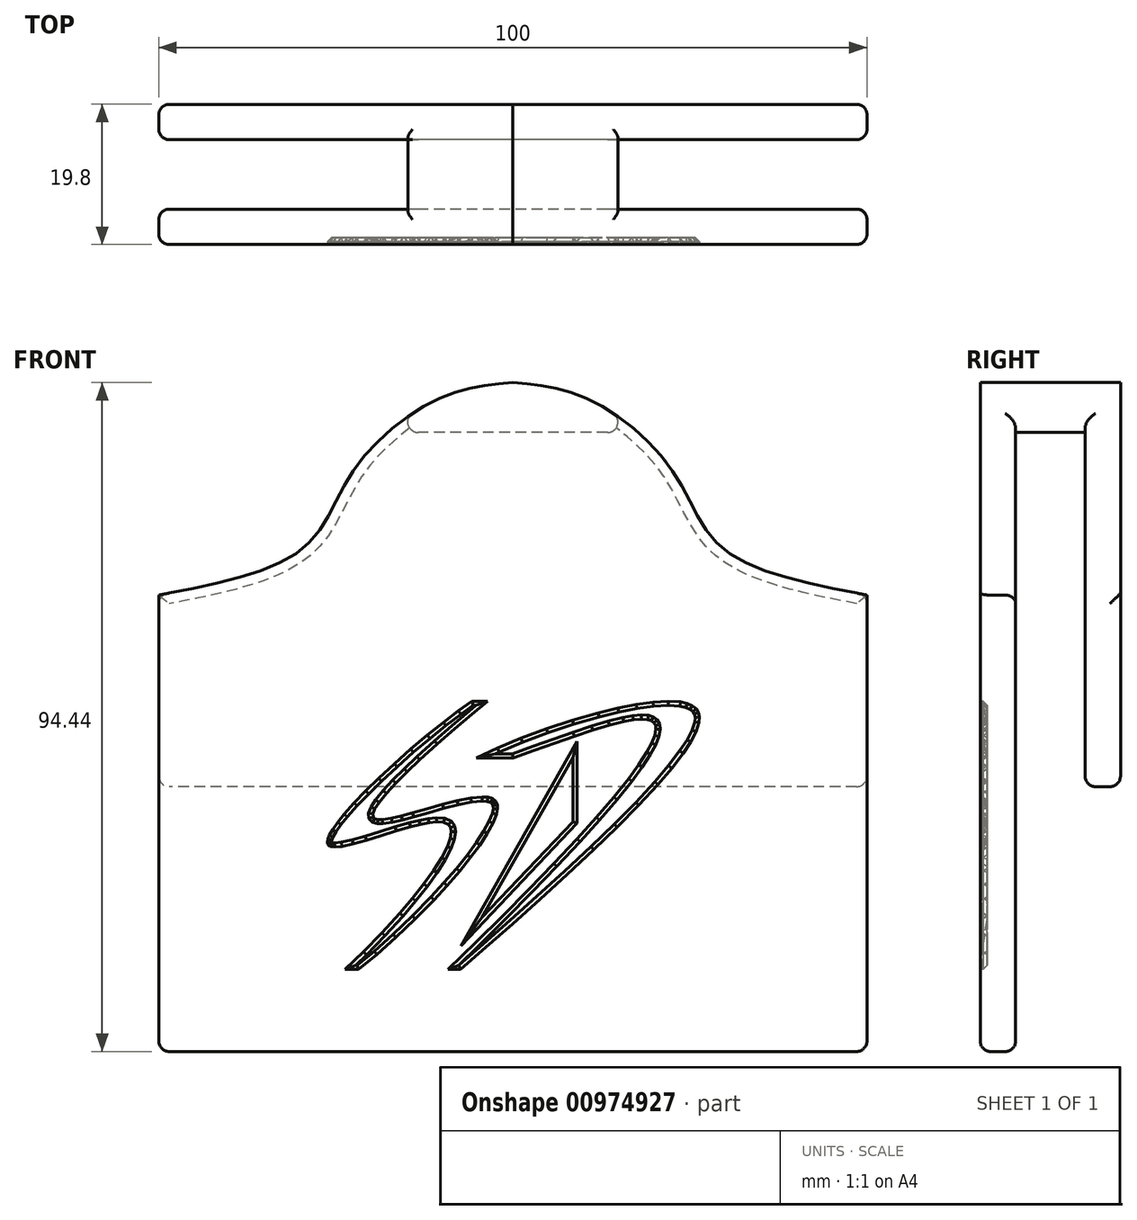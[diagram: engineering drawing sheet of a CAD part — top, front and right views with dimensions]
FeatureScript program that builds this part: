
annotation { "Feature Type Name" : "Feature", "Feature Type Description" : "" }
export const myFeature = defineFeature(function(context is Context, id is Id, definition is map)
    precondition{}
    {
        {
            var Q0;
            Q0=qCreatedBy(makeId("Right.planeOp"),FACE);
            var sketch = newSketch(context, id + "F0", { "sketchPlane" : qUnion([Q0])});
            skLineSegment(sketch, "E0.bottom", {"start": v(-5.4, 63.82) * mm, "end": v(3.6, 63.82) * mm, "construction": true});
            skLineSegment(sketch, "E0.top", {"start": v(-5.4, -23.18) * mm, "end": v(3.6, -23.18) * mm, "construction": true});
            skLineSegment(sketch, "E0.left", {"start": v(-5.4, 63.82) * mm, "end": v(-5.4, -23.18) * mm, "construction": true});
            skLineSegment(sketch, "E0.right", {"start": v(3.6, 63.82) * mm, "end": v(3.6, -23.18) * mm, "construction": true});
            skLineSegment(sketch, "E1", {"start": v(4, 14.22) * mm, "end": v(4, 64.22) * mm});
            skLineSegment(sketch, "E2", {"start": v(4, 64.22) * mm, "end": v(-5.8, 64.22) * mm});
            skLineSegment(sketch, "E3", {"start": v(-5.8, 64.22) * mm, "end": v(-5.8, -23.18) * mm});
            skLineSegment(sketch, "E4", {"start": v(-5.8, -23.18) * mm, "end": v(-10.8, -23.18) * mm});
            skLineSegment(sketch, "E5", {"start": v(-10.8, -23.18) * mm, "end": v(-10.8, 69.22) * mm});
            skLineSegment(sketch, "E6", {"start": v(-10.8, 69.22) * mm, "end": v(9, 69.22) * mm});
            skLineSegment(sketch, "E7", {"start": v(9, 69.22) * mm, "end": v(9, 14.22) * mm});
            skLineSegment(sketch, "E8", {"start": v(9, 14.22) * mm, "end": v(4, 14.22) * mm});
            skSolve(sketch);
        }
        {
            var Q0;
            Q0=makeQuery(id+"F0.imprint","IMPRINT",FACE,{"disambiguationData":[TD([[makeQuery(id+"F0.imprint","IMPRINT",EDGE,{"derivedFrom":sQuery(id+"F0.wireOp",EDGE,"E1")}),-1.0]])]});
            extrude(context, id + "F1", {"entities" : qUnion([Q0]), "depth" : 100 * mm, "offsetDistance" : 25 * mm});
        }
        {
            var Q0;
            Q0=makeQuery(id+"F1.opExtrude","SWEPT_FACE",FACE,{"disambiguationData":[OSD([sQuery(id+"F0.wireOp",EDGE,"E5")])]});
            var sketch = newSketch(context, id + "F2", { "sketchPlane" : qUnion([Q0])});
            skLineSegment(sketch, "E9", {"start": v(50, 69.22) * mm, "end": v(50, -23.18) * mm, "construction": true});
            skFitSpline(sketch, "E10", {"points": [v(0, 41.26) * mm, v(20.58, 48.07) * mm, v(27.58, 59) * mm, v(40.04, 69.22) * mm, v(50, 71.26) * mm], "startDerivative": vector(81.15, 15.4) * mm, "endDerivative": vector(46.63, 3.68) * mm});
            skFitSpline(sketch, "E11.MirrorCS", {"points": [v(100, 41.26) * mm, v(79.42, 48.07) * mm, v(72.42, 59) * mm, v(59.96, 69.22) * mm, v(50, 71.26) * mm], "startDerivative": vector(-81.15, 15.4) * mm, "endDerivative": vector(-46.63, 3.68) * mm});
            skSolve(sketch);
        }
        {
            var Q0;
            {var subQ0=sQuery(id+"F2.wireOp",EDGE,"E11.MirrorCS");var subQ1=sQuery(id+"F2.wireOp",EDGE,"E10");var subQ2=makeQuery(id+"F2.imprint","INTERSECT",VERTEX,{"derivedFrom":[subQ1,subQ0]});Q0=makeQuery(id+"F2.imprint","IMPRINT",FACE,{"disambiguationData":[TD([[makeQuery(id+"F2.imprint","IMPRINT",EDGE,{"disambiguationData":[TD([[subQ2,1.0]])],"derivedFrom":subQ1}),-1.0]])]});}
            var Q1;
            Q1=makeQuery(id+"F1.opExtrude","SWEPT_FACE",FACE,{"disambiguationData":[OSD([sQuery(id+"F0.wireOp",EDGE,"E7")])]});
            extrude(context, id + "F3", {"entities" : qUnion([Q0]), "operationType" : NewBodyOperationType.ADD, "endBound" : BoundingType.UP_TO_SURFACE, "oppositeDirection" : true, "depth" : 25 * mm, "endBoundEntityFace" : qUnion([Q1]), "offsetDistance" : 25 * mm});
        }
        {
            var Q0;
            {var subQ0=sQuery(id+"F2.wireOp",EDGE,"E10");var subQ1=sQuery(id+"F0.wireOp",EDGE,"E5");var subQ2=makeQuery(id+"F1.opExtrude","CAP_EDGE",EDGE,{"disambiguationData":[OSD([subQ1])],"isStart":true});var subQ3=makeQuery(id+"F2.imprint","INTERSECT",VERTEX,{"derivedFrom":[subQ2,subQ0]});Q0=makeQuery(id+"F2.imprint","IMPRINT",FACE,{"disambiguationData":[TD([[makeQuery(id+"F2.imprint","IMPRINT",EDGE,{"disambiguationData":[TD([[subQ3,-1.0]])],"derivedFrom":subQ0}),1.0]])]});}
            var Q1;
            {var subQ0=sQuery(id+"F2.wireOp",EDGE,"E11.MirrorCS");var subQ1=sQuery(id+"F0.wireOp",EDGE,"E5");var subQ2=makeQuery(id+"F1.opExtrude","CAP_EDGE",EDGE,{"disambiguationData":[OSD([subQ1])],"isStart":false});var subQ3=makeQuery(id+"F2.imprint","INTERSECT",VERTEX,{"derivedFrom":[subQ2,subQ0]});Q1=makeQuery(id+"F2.imprint","IMPRINT",FACE,{"disambiguationData":[TD([[makeQuery(id+"F2.imprint","IMPRINT",EDGE,{"disambiguationData":[TD([[subQ3,-1.0]])],"derivedFrom":subQ0}),-1.0]])]});}
            var Q2;
            Q2=makeQuery(id+"F3.boolean.opBoolean","MERGE",FACE,{"derivedFrom":[makeQuery(id+"F1.opExtrude","SWEPT_FACE",FACE,{"disambiguationData":[OSD([sQuery(id+"F0.wireOp",EDGE,"E7")])]}),makeQuery(id+"F3.opExtrude","CAP_FACE",FACE,{"disambiguationData":[OSD([sQuery(id+"F0.wireOp",EDGE,"E5"),sQuery(id+"F0.wireOp",EDGE,"E6"),sQuery(id+"F2.wireOp",EDGE,"E10"),sQuery(id+"F2.wireOp",EDGE,"E11.MirrorCS")])],"isStart":false})]});
            extrude(context, id + "F4", {"entities" : qUnion([Q0, Q1]), "operationType" : NewBodyOperationType.REMOVE, "endBound" : BoundingType.UP_TO_SURFACE, "oppositeDirection" : true, "depth" : 25 * mm, "endBoundEntityFace" : qUnion([Q2]), "offsetDistance" : 25 * mm});
        }
        {
            var Q0;
            Q0=makeQuery(id+"F1.opExtrude","CAP_EDGE",EDGE,{"disambiguationData":[OSD([sQuery(id+"F0.wireOp",EDGE,"E5")])],"isStart":false});
            var Q1;
            {var subQ0=sQuery(id+"F0.wireOp",EDGE,"E5");var subQ1=sQuery(id+"F2.wireOp",EDGE,"E11.MirrorCS");var subQ3=sQuery(id+"F0.wireOp",EDGE,"E3");Q1=makeQuery(id+"F4.boolean.opBoolean","COPY",EDGE,{"disambiguationData":[TD([makeQuery(id+"F1.opExtrude","SWEPT_FACE",FACE,{"disambiguationData":[OSD([subQ3])]})])],"derivedFrom":makeQuery(id+"F4.opExtrude","SWEPT_EDGE",EDGE,{"disambiguationData":[OSD([subQ0,subQ1])]})});}
            var Q2;
            Q2=makeQuery(id+"F1.opExtrude","CAP_EDGE",EDGE,{"disambiguationData":[OSD([sQuery(id+"F0.wireOp",EDGE,"E3")])],"isStart":false});
            var Q3;
            {var subQ0=sQuery(id+"F2.wireOp",EDGE,"E11.MirrorCS");Q3=makeQuery(id+"F4.boolean.opBoolean","MERGE",EDGE,{"derivedFrom":[makeQuery(id+"F3.opExtrude","CAP_EDGE",EDGE,{"disambiguationData":[OSD([subQ0])],"isStart":true})],"fromTools":[makeQuery(id+"F4.opExtrude","CAP_EDGE",EDGE,{"disambiguationData":[OSD([subQ0])],"isStart":true})]});}
            var Q4;
            Q4=makeQuery(id+"F4.boolean.opBoolean","INTERSECT",EDGE,{"derivedFrom":[makeQuery(id+"F1.opExtrude","SWEPT_FACE",FACE,{"disambiguationData":[OSD([sQuery(id+"F0.wireOp",EDGE,"E3")])]}),makeQuery(id+"F4.opExtrude","SWEPT_FACE",FACE,{"disambiguationData":[OSD([sQuery(id+"F2.wireOp",EDGE,"E11.MirrorCS")])]})]});
            var Q5;
            Q5=makeQuery(id+"F4.boolean.opBoolean","INTERSECT",EDGE,{"derivedFrom":[makeQuery(id+"F1.opExtrude","SWEPT_FACE",FACE,{"disambiguationData":[OSD([sQuery(id+"F0.wireOp",EDGE,"E2")])]}),makeQuery(id+"F4.opExtrude","SWEPT_FACE",FACE,{"disambiguationData":[OSD([sQuery(id+"F2.wireOp",EDGE,"E11.MirrorCS")])]})]});
            var Q6;
            Q6=makeQuery(id+"F4.boolean.opBoolean","INTERSECT",EDGE,{"derivedFrom":[makeQuery(id+"F1.opExtrude","SWEPT_FACE",FACE,{"disambiguationData":[OSD([sQuery(id+"F0.wireOp",EDGE,"E1")])]}),makeQuery(id+"F4.opExtrude","SWEPT_FACE",FACE,{"disambiguationData":[OSD([sQuery(id+"F2.wireOp",EDGE,"E11.MirrorCS")])]})]});
            var Q7;
            {var subQ2=sQuery(id+"F0.wireOp",EDGE,"E5");var subQ3=sQuery(id+"F0.wireOp",EDGE,"E1");var subQ4=sQuery(id+"F2.wireOp",EDGE,"E11.MirrorCS");Q7=makeQuery(id+"F4.boolean.opBoolean","COPY",EDGE,{"disambiguationData":[TD([makeQuery(id+"F1.opExtrude","SWEPT_FACE",FACE,{"disambiguationData":[OSD([subQ3])]})])],"derivedFrom":makeQuery(id+"F4.opExtrude","SWEPT_EDGE",EDGE,{"disambiguationData":[OSD([subQ2,subQ4])]})});}
            var Q8;
            {var subQ0=sQuery(id+"F2.wireOp",EDGE,"E11.MirrorCS");Q8=makeQuery(id+"F4.boolean.opBoolean","MERGE",EDGE,{"derivedFrom":[makeQuery(id+"F3.opExtrude","CAP_EDGE",EDGE,{"disambiguationData":[OSD([subQ0])],"isStart":false})],"fromTools":[makeQuery(id+"F4.opExtrude","CAP_EDGE",EDGE,{"disambiguationData":[OSD([subQ0])],"isStart":false})]});}
            var Q9;
            {var subQ0=sQuery(id+"F2.wireOp",EDGE,"E10");Q9=makeQuery(id+"F4.boolean.opBoolean","MERGE",EDGE,{"derivedFrom":[makeQuery(id+"F3.opExtrude","CAP_EDGE",EDGE,{"disambiguationData":[OSD([subQ0])],"isStart":true})],"fromTools":[makeQuery(id+"F4.opExtrude","CAP_EDGE",EDGE,{"disambiguationData":[OSD([subQ0])],"isStart":true})]});}
            var Q10;
            Q10=makeQuery(id+"F4.boolean.opBoolean","INTERSECT",EDGE,{"derivedFrom":[makeQuery(id+"F1.opExtrude","SWEPT_FACE",FACE,{"disambiguationData":[OSD([sQuery(id+"F0.wireOp",EDGE,"E3")])]}),makeQuery(id+"F4.opExtrude","SWEPT_FACE",FACE,{"disambiguationData":[OSD([sQuery(id+"F2.wireOp",EDGE,"E10")])]})]});
            var Q11;
            Q11=makeQuery(id+"F4.boolean.opBoolean","INTERSECT",EDGE,{"derivedFrom":[makeQuery(id+"F1.opExtrude","SWEPT_FACE",FACE,{"disambiguationData":[OSD([sQuery(id+"F0.wireOp",EDGE,"E1")])]}),makeQuery(id+"F4.opExtrude","SWEPT_FACE",FACE,{"disambiguationData":[OSD([sQuery(id+"F2.wireOp",EDGE,"E10")])]})]});
            var Q12;
            {var subQ0=sQuery(id+"F2.wireOp",EDGE,"E10");Q12=makeQuery(id+"F4.boolean.opBoolean","MERGE",EDGE,{"derivedFrom":[makeQuery(id+"F3.opExtrude","CAP_EDGE",EDGE,{"disambiguationData":[OSD([subQ0])],"isStart":false})],"fromTools":[makeQuery(id+"F4.opExtrude","CAP_EDGE",EDGE,{"disambiguationData":[OSD([subQ0])],"isStart":false})]});}
            var Q13;
            {var subQ0=sQuery(id+"F2.wireOp",EDGE,"E10");var subQ3=sQuery(id+"F0.wireOp",EDGE,"E5");var subQ4=sQuery(id+"F0.wireOp",EDGE,"E1");Q13=makeQuery(id+"F4.boolean.opBoolean","COPY",EDGE,{"disambiguationData":[TD([makeQuery(id+"F1.opExtrude","SWEPT_FACE",FACE,{"disambiguationData":[OSD([subQ4])]})])],"derivedFrom":makeQuery(id+"F4.opExtrude","SWEPT_EDGE",EDGE,{"disambiguationData":[OSD([subQ3,subQ0])]})});}
            var Q14;
            {var subQ0=sQuery(id+"F2.wireOp",EDGE,"E10");var subQ2=sQuery(id+"F0.wireOp",EDGE,"E5");var subQ3=sQuery(id+"F0.wireOp",EDGE,"E3");Q14=makeQuery(id+"F4.boolean.opBoolean","COPY",EDGE,{"disambiguationData":[TD([makeQuery(id+"F1.opExtrude","SWEPT_FACE",FACE,{"disambiguationData":[OSD([subQ3])]})])],"derivedFrom":makeQuery(id+"F4.opExtrude","SWEPT_EDGE",EDGE,{"disambiguationData":[OSD([subQ2,subQ0])]})});}
            var Q15;
            Q15=makeQuery(id+"F1.opExtrude","CAP_EDGE",EDGE,{"disambiguationData":[OSD([sQuery(id+"F0.wireOp",EDGE,"E5")])],"isStart":true});
            var Q16;
            Q16=makeQuery(id+"F1.opExtrude","SWEPT_EDGE",EDGE,{"disambiguationData":[OSD([sQuery(id+"F0.wireOp",EDGE,"E4"),sQuery(id+"F0.wireOp",EDGE,"E5")])]});
            var Q17;
            Q17=makeQuery(id+"F1.opExtrude","CAP_EDGE",EDGE,{"disambiguationData":[OSD([sQuery(id+"F0.wireOp",EDGE,"E1")])],"isStart":false});
            var Q18;
            Q18=makeQuery(id+"F1.opExtrude","CAP_EDGE",EDGE,{"disambiguationData":[OSD([sQuery(id+"F0.wireOp",EDGE,"E7")])],"isStart":false});
            var Q19;
            Q19=makeQuery(id+"F1.opExtrude","CAP_EDGE",EDGE,{"disambiguationData":[OSD([sQuery(id+"F0.wireOp",EDGE,"E8")])],"isStart":false});
            var Q20;
            Q20=makeQuery(id+"F1.opExtrude","CAP_EDGE",EDGE,{"disambiguationData":[OSD([sQuery(id+"F0.wireOp",EDGE,"E4")])],"isStart":false});
            var Q21;
            Q21=makeQuery(id+"F1.opExtrude","SWEPT_EDGE",EDGE,{"disambiguationData":[OSD([sQuery(id+"F0.wireOp",EDGE,"E3"),sQuery(id+"F0.wireOp",EDGE,"E4")])]});
            var Q22;
            Q22=makeQuery(id+"F1.opExtrude","SWEPT_EDGE",EDGE,{"disambiguationData":[OSD([sQuery(id+"F0.wireOp",EDGE,"E7"),sQuery(id+"F0.wireOp",EDGE,"E8")])]});
            var Q23;
            Q23=makeQuery(id+"F1.opExtrude","SWEPT_EDGE",EDGE,{"disambiguationData":[OSD([sQuery(id+"F0.wireOp",EDGE,"E1"),sQuery(id+"F0.wireOp",EDGE,"E8")])]});
            var Q24;
            Q24=makeQuery(id+"F1.opExtrude","CAP_EDGE",EDGE,{"disambiguationData":[OSD([sQuery(id+"F0.wireOp",EDGE,"E8")])],"isStart":true});
            var Q25;
            Q25=makeQuery(id+"F1.opExtrude","CAP_EDGE",EDGE,{"disambiguationData":[OSD([sQuery(id+"F0.wireOp",EDGE,"E4")])],"isStart":true});
            var Q26;
            Q26=makeQuery(id+"F1.opExtrude","CAP_EDGE",EDGE,{"disambiguationData":[OSD([sQuery(id+"F0.wireOp",EDGE,"E7")])],"isStart":true});
            var Q27;
            Q27=makeQuery(id+"F1.opExtrude","CAP_EDGE",EDGE,{"disambiguationData":[OSD([sQuery(id+"F0.wireOp",EDGE,"E1")])],"isStart":true});
            var Q28;
            Q28=makeQuery(id+"F1.opExtrude","CAP_EDGE",EDGE,{"disambiguationData":[OSD([sQuery(id+"F0.wireOp",EDGE,"E3")])],"isStart":true});
            var Q29;
            Q29=makeQuery(id+"F4.boolean.opBoolean","INTERSECT",EDGE,{"derivedFrom":[makeQuery(id+"F1.opExtrude","SWEPT_FACE",FACE,{"disambiguationData":[OSD([sQuery(id+"F0.wireOp",EDGE,"E2")])]}),makeQuery(id+"F4.opExtrude","SWEPT_FACE",FACE,{"disambiguationData":[OSD([sQuery(id+"F2.wireOp",EDGE,"E10")])]})]});
            fillet(context, id + "F5", {"entities" : qUnion([Q0, Q1, Q2, Q3, Q4, Q5, Q6, Q7, Q8, Q9, Q10, Q11, Q12, Q13, Q14, Q15, Q16, Q17, Q18, Q19, Q20, Q21, Q22, Q23, Q24, Q25, Q26, Q27, Q28, Q29]), "radius" : 1.46 * mm, "tangentPropagation" : true, "allowEdgeOverflow" : false});
        }
        {
            var Q0;
            {var subQ0=sQuery(id+"F0.wireOp",EDGE,"E5");Q0=makeQuery(id+"F3.boolean.opBoolean","MERGE",FACE,{"derivedFrom":[makeQuery(id+"F1.opExtrude","SWEPT_FACE",FACE,{"disambiguationData":[OSD([subQ0])]}),makeQuery(id+"F3.opExtrude","CAP_FACE",FACE,{"disambiguationData":[OSD([subQ0,sQuery(id+"F0.wireOp",EDGE,"E6"),sQuery(id+"F2.wireOp",EDGE,"E10"),sQuery(id+"F2.wireOp",EDGE,"E11.MirrorCS")])],"isStart":true})]});}
            var sketch = newSketch(context, id + "F6", { "sketchPlane" : qUnion([Q0])});
            skLineSegment(sketch, "E12", {"start": v(42.65, -8.3) * mm, "end": v(59.08, 9.03) * mm});
            skLineSegment(sketch, "E13", {"start": v(59.08, 20.6) * mm, "end": v(42.65, -8.3) * mm});
            skLineSegment(sketch, "E14", {"start": v(59.08, 20.6) * mm, "end": v(59.08, 9.03) * mm});
            skLineSegment(sketch, "E15", {"start": v(50.02, 18.24) * mm, "end": v(53.03, 19.32) * mm});
            skLineSegment(sketch, "E16", {"start": v(53.03, 19.32) * mm, "end": v(55.94, 20.36) * mm});
            skLineSegment(sketch, "E17", {"start": v(55.94, 20.36) * mm, "end": v(58.7, 21.33) * mm});
            skLineSegment(sketch, "E18", {"start": v(58.7, 21.33) * mm, "end": v(61.28, 22.2) * mm});
            skLineSegment(sketch, "E19", {"start": v(61.28, 22.2) * mm, "end": v(63.62, 22.9) * mm});
            skLineSegment(sketch, "E20", {"start": v(63.62, 22.9) * mm, "end": v(65.67, 23.42) * mm});
            skLineSegment(sketch, "E21", {"start": v(65.67, 23.42) * mm, "end": v(67, 23.65) * mm});
            skLineSegment(sketch, "E22", {"start": v(67, 23.65) * mm, "end": v(68.13, 23.75) * mm});
            skLineSegment(sketch, "E23", {"start": v(68.13, 23.75) * mm, "end": v(69.03, 23.68) * mm});
            skLineSegment(sketch, "E24", {"start": v(69.03, 23.68) * mm, "end": v(69.55, 23.51) * mm});
            skLineSegment(sketch, "E25", {"start": v(69.55, 23.51) * mm, "end": v(69.92, 23.24) * mm});
            skLineSegment(sketch, "E26", {"start": v(69.92, 23.24) * mm, "end": v(70.14, 22.85) * mm});
            skLineSegment(sketch, "E27", {"start": v(70.14, 22.85) * mm, "end": v(70.2, 22.34) * mm});
            skLineSegment(sketch, "E28", {"start": v(70.2, 22.34) * mm, "end": v(70.04, 21.45) * mm});
            skLineSegment(sketch, "E29", {"start": v(70.04, 21.45) * mm, "end": v(69.6, 20.35) * mm});
            skLineSegment(sketch, "E30", {"start": v(69.6, 20.35) * mm, "end": v(68.9, 19.07) * mm});
            skLineSegment(sketch, "E31", {"start": v(68.9, 19.07) * mm, "end": v(67.77, 17.32) * mm});
            skLineSegment(sketch, "E32", {"start": v(67.77, 17.32) * mm, "end": v(66.33, 15.35) * mm});
            skLineSegment(sketch, "E33", {"start": v(66.33, 15.35) * mm, "end": v(64.24, 12.75) * mm});
            skLineSegment(sketch, "E34", {"start": v(64.24, 12.75) * mm, "end": v(61.8, 9.9) * mm});
            skLineSegment(sketch, "E35", {"start": v(61.8, 9.9) * mm, "end": v(59.03, 6.83) * mm});
            skLineSegment(sketch, "E36", {"start": v(59.03, 6.83) * mm, "end": v(55.78, 3.36) * mm});
            skLineSegment(sketch, "E37", {"start": v(55.78, 3.36) * mm, "end": v(52.28, -0.27) * mm});
            skLineSegment(sketch, "E38", {"start": v(52.28, -0.27) * mm, "end": v(48.6, -4) * mm});
            skLineSegment(sketch, "E39", {"start": v(48.6, -4) * mm, "end": v(44.77, -7.8) * mm});
            skLineSegment(sketch, "E40", {"start": v(44.77, -7.8) * mm, "end": v(40.86, -11.6) * mm});
            skLineSegment(sketch, "E41", {"start": v(46.44, 26.27) * mm, "end": v(44.22, 24.43) * mm});
            skLineSegment(sketch, "E42", {"start": v(44.22, 24.43) * mm, "end": v(41.8, 22.37) * mm});
            skLineSegment(sketch, "E43", {"start": v(41.8, 22.37) * mm, "end": v(39.3, 20.2) * mm});
            skLineSegment(sketch, "E44", {"start": v(39.3, 20.2) * mm, "end": v(36.86, 18) * mm});
            skLineSegment(sketch, "E45", {"start": v(36.86, 18) * mm, "end": v(35.08, 16.32) * mm});
            skLineSegment(sketch, "E46", {"start": v(35.08, 16.32) * mm, "end": v(33.48, 14.73) * mm});
            skLineSegment(sketch, "E47", {"start": v(33.48, 14.73) * mm, "end": v(32.13, 13.27) * mm});
            skLineSegment(sketch, "E48", {"start": v(32.13, 13.27) * mm, "end": v(31.1, 12) * mm});
            skLineSegment(sketch, "E49", {"start": v(31.1, 12) * mm, "end": v(30.5, 11.08) * mm});
            skLineSegment(sketch, "E50", {"start": v(30.5, 11.08) * mm, "end": v(30.23, 10.36) * mm});
            skLineSegment(sketch, "E51", {"start": v(30.23, 10.36) * mm, "end": v(30.26, 9.96) * mm});
            skLineSegment(sketch, "E52", {"start": v(30.26, 9.96) * mm, "end": v(30.5, 9.7) * mm});
            skLineSegment(sketch, "E53", {"start": v(30.5, 9.7) * mm, "end": v(30.94, 9.58) * mm});
            skLineSegment(sketch, "E54", {"start": v(30.94, 9.58) * mm, "end": v(31.56, 9.58) * mm});
            skLineSegment(sketch, "E55", {"start": v(31.56, 9.58) * mm, "end": v(32.85, 9.77) * mm});
            skLineSegment(sketch, "E56", {"start": v(32.85, 9.77) * mm, "end": v(34.25, 10.1) * mm});
            skLineSegment(sketch, "E57", {"start": v(34.25, 10.1) * mm, "end": v(35.84, 10.52) * mm});
            skLineSegment(sketch, "E58", {"start": v(35.84, 10.52) * mm, "end": v(37.92, 11.1) * mm});
            skLineSegment(sketch, "E59", {"start": v(37.92, 11.1) * mm, "end": v(40.06, 11.7) * mm});
            skLineSegment(sketch, "E60", {"start": v(40.06, 11.7) * mm, "end": v(42.13, 12.23) * mm});
            skLineSegment(sketch, "E61", {"start": v(42.13, 12.23) * mm, "end": v(44.04, 12.6) * mm});
            skLineSegment(sketch, "E62", {"start": v(44.04, 12.6) * mm, "end": v(45.67, 12.76) * mm});
            skLineSegment(sketch, "E63", {"start": v(45.67, 12.76) * mm, "end": v(46.49, 12.71) * mm});
            skLineSegment(sketch, "E64", {"start": v(46.49, 12.71) * mm, "end": v(47.13, 12.52) * mm});
            skLineSegment(sketch, "E65", {"start": v(47.13, 12.52) * mm, "end": v(47.56, 12.18) * mm});
            skLineSegment(sketch, "E66", {"start": v(47.56, 12.18) * mm, "end": v(47.79, 11.69) * mm});
            skLineSegment(sketch, "E67", {"start": v(47.79, 11.69) * mm, "end": v(47.82, 11.05) * mm});
            skLineSegment(sketch, "E68", {"start": v(47.82, 11.05) * mm, "end": v(47.67, 10.3) * mm});
            skLineSegment(sketch, "E69", {"start": v(47.67, 10.3) * mm, "end": v(47.18, 9.03) * mm});
            skLineSegment(sketch, "E70", {"start": v(47.18, 9.03) * mm, "end": v(46.39, 7.57) * mm});
            skLineSegment(sketch, "E71", {"start": v(46.39, 7.57) * mm, "end": v(45.33, 5.95) * mm});
            skLineSegment(sketch, "E72", {"start": v(45.33, 5.95) * mm, "end": v(44.03, 4.2) * mm});
            skLineSegment(sketch, "E73", {"start": v(44.03, 4.2) * mm, "end": v(42.47, 2.26) * mm});
            skLineSegment(sketch, "E74", {"start": v(42.47, 2.26) * mm, "end": v(40.74, 0.26) * mm});
            skLineSegment(sketch, "E75", {"start": v(40.74, 0.26) * mm, "end": v(38.87, -1.78) * mm});
            skLineSegment(sketch, "E76", {"start": v(38.87, -1.78) * mm, "end": v(36.22, -4.48) * mm});
            skLineSegment(sketch, "E77", {"start": v(36.22, -4.48) * mm, "end": v(33.5, -7.09) * mm});
            skLineSegment(sketch, "E78", {"start": v(33.5, -7.09) * mm, "end": v(30.8, -9.49) * mm});
            skLineSegment(sketch, "E79", {"start": v(30.8, -9.49) * mm, "end": v(28.22, -11.6) * mm});
            skLineSegment(sketch, "E80", {"start": v(44.2, 26.27) * mm, "end": v(42.3, 24.92) * mm});
            skLineSegment(sketch, "E81", {"start": v(42.3, 24.92) * mm, "end": v(40.17, 23.3) * mm});
            skLineSegment(sketch, "E82", {"start": v(40.17, 23.3) * mm, "end": v(37.91, 21.48) * mm});
            skLineSegment(sketch, "E83", {"start": v(37.91, 21.48) * mm, "end": v(35.59, 19.51) * mm});
            skLineSegment(sketch, "E84", {"start": v(35.59, 19.51) * mm, "end": v(33.27, 17.46) * mm});
            skLineSegment(sketch, "E85", {"start": v(33.27, 17.46) * mm, "end": v(31.05, 15.4) * mm});
            skLineSegment(sketch, "E86", {"start": v(31.05, 15.4) * mm, "end": v(29.23, 13.62) * mm});
            skLineSegment(sketch, "E87", {"start": v(29.23, 13.62) * mm, "end": v(27.59, 11.91) * mm});
            skLineSegment(sketch, "E88", {"start": v(27.59, 11.91) * mm, "end": v(26.18, 10.33) * mm});
            skLineSegment(sketch, "E89", {"start": v(26.18, 10.33) * mm, "end": v(25.26, 9.2) * mm});
            skLineSegment(sketch, "E90", {"start": v(25.26, 9.2) * mm, "end": v(24.55, 8.2) * mm});
            skLineSegment(sketch, "E91", {"start": v(24.55, 8.2) * mm, "end": v(24.05, 7.33) * mm});
            skLineSegment(sketch, "E92", {"start": v(24.05, 7.33) * mm, "end": v(23.87, 6.85) * mm});
            skLineSegment(sketch, "E93", {"start": v(23.87, 6.85) * mm, "end": v(23.8, 6.45) * mm});
            skLineSegment(sketch, "E94", {"start": v(23.8, 6.45) * mm, "end": v(23.83, 6.13) * mm});
            skLineSegment(sketch, "E95", {"start": v(23.83, 6.13) * mm, "end": v(24, 5.9) * mm});
            skLineSegment(sketch, "E96", {"start": v(24, 5.9) * mm, "end": v(24.34, 5.74) * mm});
            skLineSegment(sketch, "E97", {"start": v(24.34, 5.74) * mm, "end": v(24.82, 5.68) * mm});
            skLineSegment(sketch, "E98", {"start": v(24.82, 5.68) * mm, "end": v(25.85, 5.78) * mm});
            skLineSegment(sketch, "E99", {"start": v(25.85, 5.78) * mm, "end": v(27.46, 6.13) * mm});
            skLineSegment(sketch, "E100", {"start": v(27.46, 6.13) * mm, "end": v(29.34, 6.66) * mm});
            skLineSegment(sketch, "E101", {"start": v(29.34, 6.66) * mm, "end": v(31.4, 7.3) * mm});
            skLineSegment(sketch, "E102", {"start": v(31.4, 7.3) * mm, "end": v(33.5, 7.95) * mm});
            skLineSegment(sketch, "E103", {"start": v(33.5, 7.95) * mm, "end": v(35.56, 8.54) * mm});
            skLineSegment(sketch, "E104", {"start": v(35.56, 8.54) * mm, "end": v(36.91, 8.88) * mm});
            skLineSegment(sketch, "E105", {"start": v(36.91, 8.88) * mm, "end": v(38.14, 9.12) * mm});
            skLineSegment(sketch, "E106", {"start": v(38.14, 9.12) * mm, "end": v(39.21, 9.23) * mm});
            skLineSegment(sketch, "E107", {"start": v(39.21, 9.23) * mm, "end": v(40.23, 9.16) * mm});
            skLineSegment(sketch, "E108", {"start": v(40.23, 9.16) * mm, "end": v(40.9, 8.83) * mm});
            skLineSegment(sketch, "E109", {"start": v(40.9, 8.83) * mm, "end": v(41.2, 8.4) * mm});
            skLineSegment(sketch, "E110", {"start": v(41.2, 8.4) * mm, "end": v(41.3, 7.85) * mm});
            skLineSegment(sketch, "E111", {"start": v(41.3, 7.85) * mm, "end": v(41.16, 6.9) * mm});
            skLineSegment(sketch, "E112", {"start": v(41.16, 6.9) * mm, "end": v(40.75, 5.77) * mm});
            skLineSegment(sketch, "E113", {"start": v(40.75, 5.77) * mm, "end": v(39.93, 4.18) * mm});
            skLineSegment(sketch, "E114", {"start": v(39.93, 4.18) * mm, "end": v(38.8, 2.4) * mm});
            skLineSegment(sketch, "E115", {"start": v(38.8, 2.4) * mm, "end": v(37.41, 0.46) * mm});
            skLineSegment(sketch, "E116", {"start": v(37.41, 0.46) * mm, "end": v(35.8, -1.58) * mm});
            skLineSegment(sketch, "E117", {"start": v(35.8, -1.58) * mm, "end": v(34.02, -3.68) * mm});
            skLineSegment(sketch, "E118", {"start": v(34.02, -3.68) * mm, "end": v(31.52, -6.44) * mm});
            skLineSegment(sketch, "E119", {"start": v(31.52, -6.44) * mm, "end": v(28.91, -9.11) * mm});
            skLineSegment(sketch, "E120", {"start": v(28.91, -9.11) * mm, "end": v(26.31, -11.6) * mm});
            skLineSegment(sketch, "E121", {"start": v(44.83, 18.24) * mm, "end": v(47.81, 19.65) * mm});
            skLineSegment(sketch, "E122", {"start": v(47.81, 19.65) * mm, "end": v(51.15, 21.05) * mm});
            skLineSegment(sketch, "E123", {"start": v(51.15, 21.05) * mm, "end": v(54.72, 22.38) * mm});
            skLineSegment(sketch, "E124", {"start": v(54.72, 22.38) * mm, "end": v(58.4, 23.6) * mm});
            skLineSegment(sketch, "E125", {"start": v(58.4, 23.6) * mm, "end": v(62.04, 24.64) * mm});
            skLineSegment(sketch, "E126", {"start": v(62.04, 24.64) * mm, "end": v(64.8, 25.31) * mm});
            skLineSegment(sketch, "E127", {"start": v(64.8, 25.31) * mm, "end": v(67.42, 25.83) * mm});
            skLineSegment(sketch, "E128", {"start": v(67.42, 25.83) * mm, "end": v(69.8, 26.16) * mm});
            skLineSegment(sketch, "E129", {"start": v(69.8, 26.16) * mm, "end": v(71.92, 26.28) * mm});
            skLineSegment(sketch, "E130", {"start": v(71.92, 26.28) * mm, "end": v(73.69, 26.17) * mm});
            skLineSegment(sketch, "E131", {"start": v(73.69, 26.17) * mm, "end": v(74.6, 25.97) * mm});
            skLineSegment(sketch, "E132", {"start": v(74.6, 25.97) * mm, "end": v(75.33, 25.66) * mm});
            skLineSegment(sketch, "E133", {"start": v(75.33, 25.66) * mm, "end": v(75.87, 25.23) * mm});
            skLineSegment(sketch, "E134", {"start": v(75.87, 25.23) * mm, "end": v(76.2, 24.69) * mm});
            skLineSegment(sketch, "E135", {"start": v(76.2, 24.69) * mm, "end": v(76.34, 24.03) * mm});
            skLineSegment(sketch, "E136", {"start": v(76.34, 24.03) * mm, "end": v(76.27, 23.25) * mm});
            skLineSegment(sketch, "E137", {"start": v(76.27, 23.25) * mm, "end": v(75.86, 21.98) * mm});
            skLineSegment(sketch, "E138", {"start": v(75.86, 21.98) * mm, "end": v(75.1, 20.53) * mm});
            skLineSegment(sketch, "E139", {"start": v(75.1, 20.53) * mm, "end": v(74.05, 18.9) * mm});
            skLineSegment(sketch, "E140", {"start": v(74.05, 18.9) * mm, "end": v(72.44, 16.8) * mm});
            skLineSegment(sketch, "E141", {"start": v(72.44, 16.8) * mm, "end": v(70.49, 14.5) * mm});
            skLineSegment(sketch, "E142", {"start": v(70.49, 14.5) * mm, "end": v(67.78, 11.57) * mm});
            skLineSegment(sketch, "E143", {"start": v(67.78, 11.57) * mm, "end": v(64.74, 8.49) * mm});
            skLineSegment(sketch, "E144", {"start": v(64.74, 8.49) * mm, "end": v(61.43, 5.29) * mm});
            skLineSegment(sketch, "E145", {"start": v(61.43, 5.29) * mm, "end": v(57.69, 1.8) * mm});
            skLineSegment(sketch, "E146", {"start": v(57.69, 1.8) * mm, "end": v(53.83, -1.7) * mm});
            skLineSegment(sketch, "E147", {"start": v(53.83, -1.7) * mm, "end": v(49.97, -5.14) * mm});
            skLineSegment(sketch, "E148", {"start": v(49.97, -5.14) * mm, "end": v(46.2, -8.46) * mm});
            skLineSegment(sketch, "E149", {"start": v(46.2, -8.46) * mm, "end": v(42.6, -11.6) * mm});
            skLineSegment(sketch, "E150", {"start": v(44.83, 18.24) * mm, "end": v(50.02, 18.24) * mm});
            skLineSegment(sketch, "E151", {"start": v(40.86, -11.6) * mm, "end": v(42.6, -11.6) * mm});
            skLineSegment(sketch, "E152", {"start": v(26.31, -11.6) * mm, "end": v(28.22, -11.6) * mm});
            skLineSegment(sketch, "E153", {"start": v(44.2, 26.27) * mm, "end": v(46.44, 26.27) * mm});
            skLineSegment(sketch, "E154", {"start": v(1.46, 9.17) * mm, "end": v(98.54, 9.17) * mm, "construction": true});
            skLineSegment(sketch, "E155", {"start": v(50, 69.79) * mm, "end": v(50.84, -21.72) * mm, "construction": true});
            skSolve(sketch);
        }
        {
            var Q0;
            Q0 = qSketchRegion(id + "F6", true);
            extrude(context, id + "F7", {"entities" : qUnion([Q0]), "operationType" : NewBodyOperationType.REMOVE, "oppositeDirection" : true, "depth" : 1 * mm, "offsetDistance" : 25 * mm});
        }
        {
            var Q0;
            Q0=makeQuery(id+"F7.boolean.opBoolean","COPY",FACE,{"derivedFrom":makeQuery(id+"F7.opExtrude","CAP_FACE",FACE,{"disambiguationData":[OSD([sQuery(id+"F6.wireOp",EDGE,"E41"),sQuery(id+"F6.wireOp",EDGE,"E42"),sQuery(id+"F6.wireOp",EDGE,"E43"),sQuery(id+"F6.wireOp",EDGE,"E44"),sQuery(id+"F6.wireOp",EDGE,"E45"),sQuery(id+"F6.wireOp",EDGE,"E46"),sQuery(id+"F6.wireOp",EDGE,"E47"),sQuery(id+"F6.wireOp",EDGE,"E48"),sQuery(id+"F6.wireOp",EDGE,"E49"),sQuery(id+"F6.wireOp",EDGE,"E50"),sQuery(id+"F6.wireOp",EDGE,"E51"),sQuery(id+"F6.wireOp",EDGE,"E52"),sQuery(id+"F6.wireOp",EDGE,"E53"),sQuery(id+"F6.wireOp",EDGE,"E54"),sQuery(id+"F6.wireOp",EDGE,"E55"),sQuery(id+"F6.wireOp",EDGE,"E56"),sQuery(id+"F6.wireOp",EDGE,"E57"),sQuery(id+"F6.wireOp",EDGE,"E58"),sQuery(id+"F6.wireOp",EDGE,"E59"),sQuery(id+"F6.wireOp",EDGE,"E60"),sQuery(id+"F6.wireOp",EDGE,"E61"),sQuery(id+"F6.wireOp",EDGE,"E62"),sQuery(id+"F6.wireOp",EDGE,"E63"),sQuery(id+"F6.wireOp",EDGE,"E64"),sQuery(id+"F6.wireOp",EDGE,"E65"),sQuery(id+"F6.wireOp",EDGE,"E66"),sQuery(id+"F6.wireOp",EDGE,"E67"),sQuery(id+"F6.wireOp",EDGE,"E68"),sQuery(id+"F6.wireOp",EDGE,"E69"),sQuery(id+"F6.wireOp",EDGE,"E70"),sQuery(id+"F6.wireOp",EDGE,"E71"),sQuery(id+"F6.wireOp",EDGE,"E72"),sQuery(id+"F6.wireOp",EDGE,"E73"),sQuery(id+"F6.wireOp",EDGE,"E74"),sQuery(id+"F6.wireOp",EDGE,"E75"),sQuery(id+"F6.wireOp",EDGE,"E76"),sQuery(id+"F6.wireOp",EDGE,"E77"),sQuery(id+"F6.wireOp",EDGE,"E78"),sQuery(id+"F6.wireOp",EDGE,"E79"),sQuery(id+"F6.wireOp",EDGE,"E80"),sQuery(id+"F6.wireOp",EDGE,"E81"),sQuery(id+"F6.wireOp",EDGE,"E82"),sQuery(id+"F6.wireOp",EDGE,"E83"),sQuery(id+"F6.wireOp",EDGE,"E84"),sQuery(id+"F6.wireOp",EDGE,"E85"),sQuery(id+"F6.wireOp",EDGE,"E86"),sQuery(id+"F6.wireOp",EDGE,"E87"),sQuery(id+"F6.wireOp",EDGE,"E88"),sQuery(id+"F6.wireOp",EDGE,"E89"),sQuery(id+"F6.wireOp",EDGE,"E90"),sQuery(id+"F6.wireOp",EDGE,"E91"),sQuery(id+"F6.wireOp",EDGE,"E92"),sQuery(id+"F6.wireOp",EDGE,"E93"),sQuery(id+"F6.wireOp",EDGE,"E94"),sQuery(id+"F6.wireOp",EDGE,"E95"),sQuery(id+"F6.wireOp",EDGE,"E96"),sQuery(id+"F6.wireOp",EDGE,"E97"),sQuery(id+"F6.wireOp",EDGE,"E98"),sQuery(id+"F6.wireOp",EDGE,"E99"),sQuery(id+"F6.wireOp",EDGE,"E100"),sQuery(id+"F6.wireOp",EDGE,"E101"),sQuery(id+"F6.wireOp",EDGE,"E102"),sQuery(id+"F6.wireOp",EDGE,"E103"),sQuery(id+"F6.wireOp",EDGE,"E104"),sQuery(id+"F6.wireOp",EDGE,"E105"),sQuery(id+"F6.wireOp",EDGE,"E106"),sQuery(id+"F6.wireOp",EDGE,"E107"),sQuery(id+"F6.wireOp",EDGE,"E108"),sQuery(id+"F6.wireOp",EDGE,"E109"),sQuery(id+"F6.wireOp",EDGE,"E110"),sQuery(id+"F6.wireOp",EDGE,"E111"),sQuery(id+"F6.wireOp",EDGE,"E112"),sQuery(id+"F6.wireOp",EDGE,"E113"),sQuery(id+"F6.wireOp",EDGE,"E114"),sQuery(id+"F6.wireOp",EDGE,"E115"),sQuery(id+"F6.wireOp",EDGE,"E116"),sQuery(id+"F6.wireOp",EDGE,"E117"),sQuery(id+"F6.wireOp",EDGE,"E118"),sQuery(id+"F6.wireOp",EDGE,"E119"),sQuery(id+"F6.wireOp",EDGE,"E120"),sQuery(id+"F6.wireOp",EDGE,"E152"),sQuery(id+"F6.wireOp",EDGE,"E153")])],"isStart":false})});
            var Q1;
            Q1=makeQuery(id+"F7.boolean.opBoolean","COPY",FACE,{"derivedFrom":makeQuery(id+"F7.opExtrude","CAP_FACE",FACE,{"disambiguationData":[OSD([sQuery(id+"F6.wireOp",EDGE,"E15"),sQuery(id+"F6.wireOp",EDGE,"E16"),sQuery(id+"F6.wireOp",EDGE,"E17"),sQuery(id+"F6.wireOp",EDGE,"E18"),sQuery(id+"F6.wireOp",EDGE,"E19"),sQuery(id+"F6.wireOp",EDGE,"E20"),sQuery(id+"F6.wireOp",EDGE,"E21"),sQuery(id+"F6.wireOp",EDGE,"E22"),sQuery(id+"F6.wireOp",EDGE,"E23"),sQuery(id+"F6.wireOp",EDGE,"E24"),sQuery(id+"F6.wireOp",EDGE,"E25"),sQuery(id+"F6.wireOp",EDGE,"E26"),sQuery(id+"F6.wireOp",EDGE,"E27"),sQuery(id+"F6.wireOp",EDGE,"E28"),sQuery(id+"F6.wireOp",EDGE,"E29"),sQuery(id+"F6.wireOp",EDGE,"E30"),sQuery(id+"F6.wireOp",EDGE,"E31"),sQuery(id+"F6.wireOp",EDGE,"E32"),sQuery(id+"F6.wireOp",EDGE,"E33"),sQuery(id+"F6.wireOp",EDGE,"E34"),sQuery(id+"F6.wireOp",EDGE,"E35"),sQuery(id+"F6.wireOp",EDGE,"E36"),sQuery(id+"F6.wireOp",EDGE,"E37"),sQuery(id+"F6.wireOp",EDGE,"E38"),sQuery(id+"F6.wireOp",EDGE,"E39"),sQuery(id+"F6.wireOp",EDGE,"E40"),sQuery(id+"F6.wireOp",EDGE,"E121"),sQuery(id+"F6.wireOp",EDGE,"E122"),sQuery(id+"F6.wireOp",EDGE,"E123"),sQuery(id+"F6.wireOp",EDGE,"E124"),sQuery(id+"F6.wireOp",EDGE,"E125"),sQuery(id+"F6.wireOp",EDGE,"E126"),sQuery(id+"F6.wireOp",EDGE,"E127"),sQuery(id+"F6.wireOp",EDGE,"E128"),sQuery(id+"F6.wireOp",EDGE,"E129"),sQuery(id+"F6.wireOp",EDGE,"E130"),sQuery(id+"F6.wireOp",EDGE,"E131"),sQuery(id+"F6.wireOp",EDGE,"E132"),sQuery(id+"F6.wireOp",EDGE,"E133"),sQuery(id+"F6.wireOp",EDGE,"E134"),sQuery(id+"F6.wireOp",EDGE,"E135"),sQuery(id+"F6.wireOp",EDGE,"E136"),sQuery(id+"F6.wireOp",EDGE,"E137"),sQuery(id+"F6.wireOp",EDGE,"E138"),sQuery(id+"F6.wireOp",EDGE,"E139"),sQuery(id+"F6.wireOp",EDGE,"E140"),sQuery(id+"F6.wireOp",EDGE,"E141"),sQuery(id+"F6.wireOp",EDGE,"E142"),sQuery(id+"F6.wireOp",EDGE,"E143"),sQuery(id+"F6.wireOp",EDGE,"E144"),sQuery(id+"F6.wireOp",EDGE,"E145"),sQuery(id+"F6.wireOp",EDGE,"E146"),sQuery(id+"F6.wireOp",EDGE,"E147"),sQuery(id+"F6.wireOp",EDGE,"E148"),sQuery(id+"F6.wireOp",EDGE,"E149"),sQuery(id+"F6.wireOp",EDGE,"E150"),sQuery(id+"F6.wireOp",EDGE,"E151")])],"isStart":false})});
            var Q2;
            Q2=makeQuery(id+"F7.boolean.opBoolean","COPY",FACE,{"derivedFrom":makeQuery(id+"F7.opExtrude","CAP_FACE",FACE,{"disambiguationData":[OSD([sQuery(id+"F6.wireOp",EDGE,"E12"),sQuery(id+"F6.wireOp",EDGE,"E13"),sQuery(id+"F6.wireOp",EDGE,"E14")])],"isStart":false})});
            chamfer(context, id + "F8", {"entities" : qUnion([Q0, Q1, Q2]), "width" : 0.6 * mm, "tangentPropagation" : true});
        }
    });
